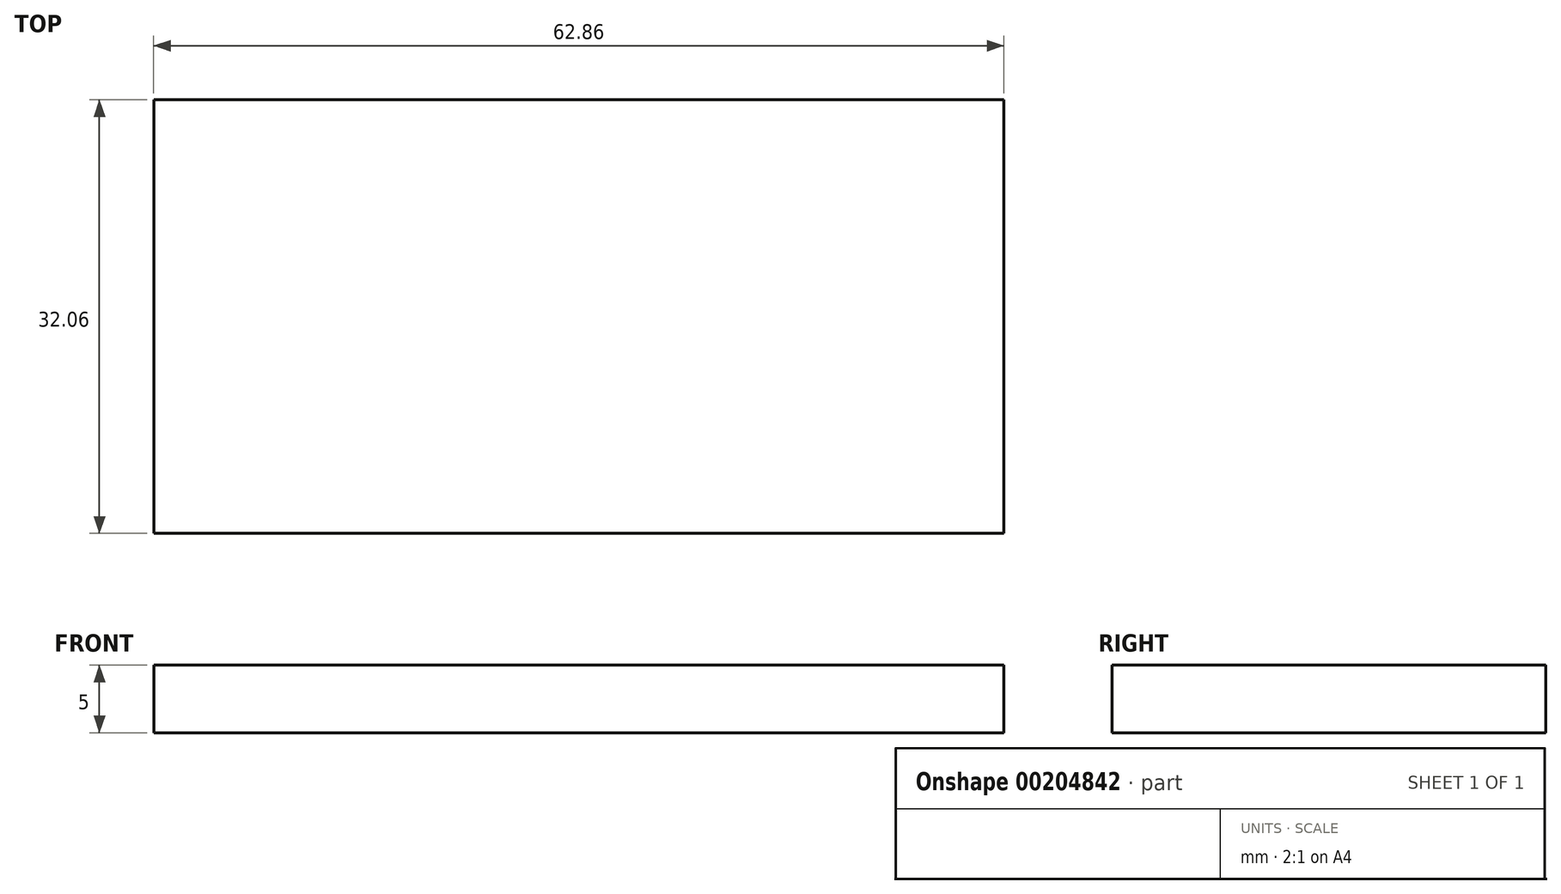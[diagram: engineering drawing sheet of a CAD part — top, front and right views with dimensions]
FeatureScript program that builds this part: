
annotation { "Feature Type Name" : "Feature", "Feature Type Description" : "" }
export const myFeature = defineFeature(function(context is Context, id is Id, definition is map)
    precondition{}
    {
        {
            var Q0;
            Q0=qCreatedBy(makeId("Top.planeOp"),FACE);
            var sketch = newSketch(context, id + "F0", { "sketchPlane" : qUnion([Q0])});
            skLineSegment(sketch, "E0.bottom", {"start": v(31.43, -16.03) * mm, "end": v(-31.43, -16.03) * mm});
            skLineSegment(sketch, "E0.top", {"start": v(31.43, 16.03) * mm, "end": v(-31.43, 16.03) * mm});
            skLineSegment(sketch, "E0.left", {"start": v(31.43, -16.03) * mm, "end": v(31.43, 16.03) * mm});
            skLineSegment(sketch, "E0.right", {"start": v(-31.43, -16.03) * mm, "end": v(-31.43, 16.03) * mm});
            skPoint(sketch, "E0.middle", {"position": v(0, 0) * mm});
            skSolve(sketch);
        }
        {
            var Q0;
            Q0=makeQuery(id+"F0.imprint","IMPRINT",FACE,{"disambiguationData":[TD([[makeQuery(id+"F0.imprint","IMPRINT",EDGE,{"derivedFrom":sQuery(id+"F0.wireOp",EDGE,"E0.bottom")}),-1.0]])]});
            extrude(context, id + "F1", {"entities" : qUnion([Q0]), "depth" : 5 * mm});
        }
    });
